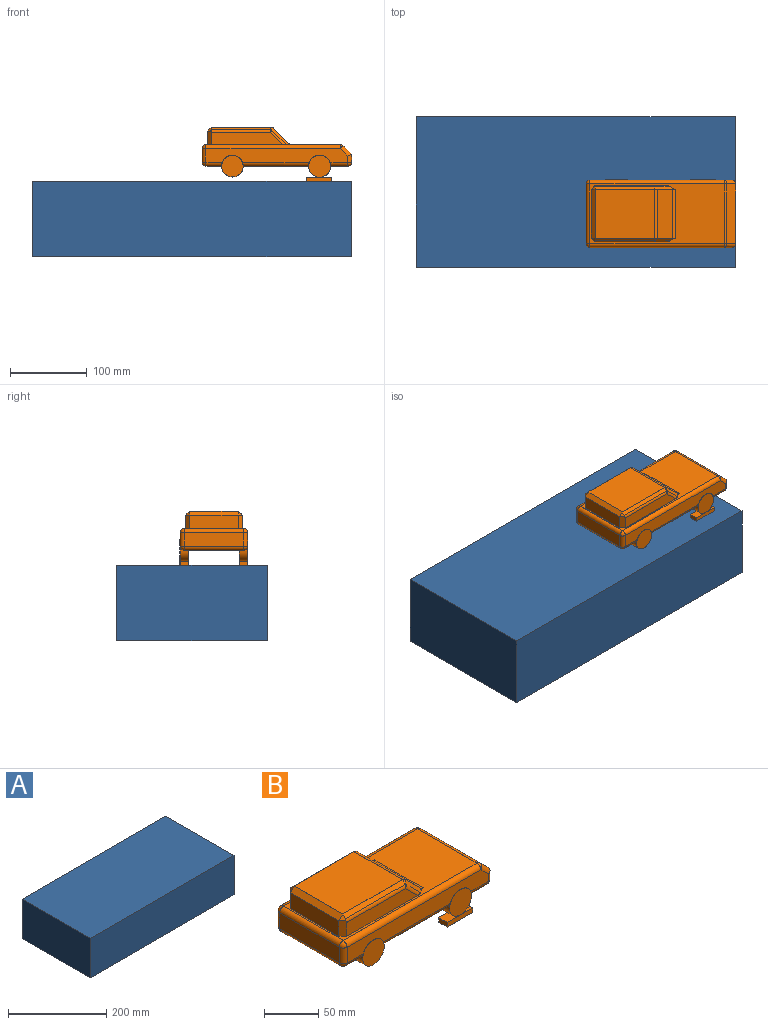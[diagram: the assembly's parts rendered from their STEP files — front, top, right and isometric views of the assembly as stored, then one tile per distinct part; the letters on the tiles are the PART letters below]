
ASSEMBLY  parts=2 mates=1
PART A: 6 faces, bbox 414.3x196x98.3 mm
  f0: plane 414.29x98.32mm, normal (0,-1,0), area 40735mm2, adj f1,f3,f4,f5
  f1: plane 195.96x98.32mm, normal (1,0,0), area 19267.6mm2, adj f0,f2,f4,f5
  f2: plane 414.29x98.32mm, normal (0,1,0), area 40735mm2, adj f1,f3,f4,f5
  f3: plane 195.96x98.32mm, normal (-1,0,0), area 19267.6mm2, adj f0,f2,f4,f5
  f4: plane 414.29x195.96mm, normal (0,0,-1), area 81185.5mm2, adj f0,f1,f2,f3
  f5: plane 414.29x195.96mm, normal (0,0,1), area 81185.5mm2, adj f0,f1,f2,f3
PART B: 166 faces, bbox 195.9x89.8x71.9 mm
  f0: plane 19.88x19.88mm, normal (0.71,0,0.71), area 1mm2, adj f17,f18,f30,f121
  f1: cylinder r=5.08mm len=86.98mm, axis (-1,0,0), area 686.5mm2, adj f3,f8,f72,f75
  f2: cylinder r=5.08mm len=21.19mm, axis (-1,0,0), area 165.3mm2, adj f3,f8,f48,f72
  f3: plane 184.14x77.67mm, normal (0,0,-1), area 13664.9mm2, adj f1,f2,f4,f5,f6,f42,f52,f53
  f4: cylinder r=5.08mm len=86.98mm, axis (1,0,0), area 686.5mm2, adj f3,f10,f61,f64
  f5: cylinder r=5.08mm len=23.05mm, axis (1,0,0), area 180.2mm2, adj f3,f10,f49,f64
  f6: cylinder r=5.08mm len=21.19mm, axis (1,0,0), area 165.3mm2, adj f3,f10,f40,f61
  f7: plane 77.67x10.16mm, normal (1,0,0), area 789.1mm2, adj f32,f43,f53,f58
  f8: plane 184.14x17.78mm, normal (0,1,0), area 2877.3mm2, adj f1,f2,f47,f52,f55,f58,f59,f72
  f9: plane 77.67x17.78mm, normal (-1,0,0), area 1381mm2, adj f39,f42,f46,f47
  f10: plane 184.14x17.78mm, normal (0,-1,0), area 2877.3mm2, adj f4,f5,f6,f39,f43,f44,f45,f61
  f11: plane 175.98x79.23mm, normal (0,0,1), area 5581.3mm2, adj f12,f13,f14,f17,f19,f20,f22,f25
  f12: plane 92.44x15.68mm, normal (0,1,0), area 1326.2mm2, adj f11,f22,f33,f35
  f13: plane 63.17x17.78mm, normal (-1,0,0), area 1123.1mm2, adj f11,f22,f25,f26
  f14: plane 92.44x15.68mm, normal (0,-1,0), area 1326.2mm2, adj f11,f25,f36,f37
  f15: plane 77.63x63.17mm, normal (0,0,1), area 4903.8mm2, adj f18,f23,f26,f28
  f16: plane 19.88x19.88mm, normal (0.71,0,0.71), area 1mm2, adj f17,f18,f20,f131
  f17: cylinder r=5.08mm len=63.17mm, axis (0,-1,0), area 252mm2, adj f0,f11,f16,f19,f31,f151
  f18: cylinder r=5.08mm len=63.17mm, axis (0,-1,0), area 252mm2, adj f0,f15,f16,f21,f29,f150
  f19: cone r=10.16mm half-angle=45deg, axis (0,1,0), area 6.8mm2, adj f11,f17,f20
  f20: plane 22.42x21.37mm, normal (0.5,0.71,0.5), area 141.3mm2, adj f11,f16,f19,f21,f33
  f21: cone r=5.08mm half-angle=45deg, axis (0,-1,0), area 13.1mm2, adj f18,f20,f23,f34
  f22: plane 18.01x5.31mm, normal (-0.71,0.71,0), area 127.3mm2, adj f11,f12,f13,f24,f35
  f23: plane 77.63x3.59mm, normal (0,0.71,0.71), area 394.4mm2, adj f15,f21,f24,f35
  f24: plane 5.31x5.31mm, normal (-0.58,0.58,0.58), area 21.9mm2, adj f22,f23,f26,f35
  f25: plane 18.01x5.31mm, normal (-0.71,-0.71,0), area 127.3mm2, adj f11,f13,f14,f27,f37
  f26: plane 63.17x5.08mm, normal (-0.71,0,0.71), area 453.8mm2, adj f13,f15,f24,f27
  f27: plane 5.31x5.31mm, normal (-0.58,-0.58,0.58), area 21.9mm2, adj f25,f26,f28,f37
  f28: plane 77.63x3.59mm, normal (0,-0.71,0.71), area 394.4mm2, adj f15,f27,f29,f37
  f29: cone r=5.08mm half-angle=45deg, axis (0,1,0), area 13.1mm2, adj f18,f28,f30,f38
  f30: plane 22.42x21.37mm, normal (0.5,-0.71,0.5), area 141.3mm2, adj f0,f11,f29,f31,f36
  f31: cone r=10.16mm half-angle=45deg, axis (0,-1,0), area 6.8mm2, adj f11,f17,f30
  f32: plane 77.67x11.21mm, normal (0.71,0,0.71), area 1231.6mm2, adj f7,f44,f54,f59
  f33: cylinder r=5.08mm len=21.37mm, axis (0.71,0,-0.71), area 97.4mm2, adj f11,f12,f20,f34
  f34: bspline ~3.59x1.92mm, area 1.2mm2, adj f21,f33,f35
  f35: cylinder r=5.08mm len=78.09mm, axis (-1,0,0), area 308.9mm2, adj f12,f22,f23,f24,f34
  f36: cylinder r=5.08mm len=21.37mm, axis (-0.71,0,0.71), area 97.4mm2, adj f11,f14,f30,f38
  f37: cylinder r=5.08mm len=78.09mm, axis (1,0,0), area 308.9mm2, adj f14,f25,f27,f28,f38
  f38: bspline ~3.59x1.92mm, area 1.2mm2, adj f29,f36,f37
  f39: cylinder r=5.08mm len=17.78mm, axis (0,0,1), area 141.9mm2, adj f9,f10,f40,f41
  f40: sphere r=5.08mm, area 40.5mm2, adj f6,f39,f42
  f41: sphere r=5.08mm, area 40.5mm2, adj f39,f45,f46
  f42: cylinder r=5.08mm len=77.67mm, axis (0,-1,0), area 619.8mm2, adj f3,f9,f40,f48
  f43: cylinder r=5.08mm len=10.16mm, axis (0,0,-1), area 72.7mm2, adj f7,f10,f44,f49
  f44: cylinder r=5.08mm len=14.8mm, axis (0.71,0,-0.71), area 118.1mm2, adj f10,f32,f43,f50
  f45: cylinder r=5.08mm len=174.42mm, axis (-1,0,0), area 1391.8mm2, adj f10,f11,f41,f50
  f46: cylinder r=5.08mm len=77.67mm, axis (0,1,0), area 619.8mm2, adj f9,f11,f41,f51
  f47: cylinder r=5.08mm len=17.78mm, axis (0,0,-1), area 141.9mm2, adj f8,f9,f48,f51
  f48: sphere r=5.08mm, area 40.5mm2, adj f2,f42,f47
  f49: sphere r=5.08mm, area 40.5mm2, adj f5,f43,f53
  f50: sphere r=5.08mm, area 20.3mm2, adj f44,f45,f54
  f51: sphere r=5.08mm, area 40.5mm2, adj f46,f47,f55
  f52: cylinder r=5.08mm len=23.05mm, axis (-1,0,0), area 180.2mm2, adj f3,f8,f56,f75
  f53: cylinder r=5.08mm len=77.67mm, axis (0,1,0), area 619.8mm2, adj f3,f7,f49,f56
  f54: cylinder r=5.08mm len=77.67mm, axis (0,-1,0), area 309.9mm2, adj f11,f32,f50,f57
  f55: cylinder r=5.08mm len=174.42mm, axis (1,0,0), area 1391.8mm2, adj f8,f11,f51,f57
  f56: sphere r=5.08mm, area 40.5mm2, adj f52,f53,f58
  f57: sphere r=5.08mm, area 25.4mm2, adj f54,f55,f59
  f58: cylinder r=5.08mm len=10.16mm, axis (0,0,1), area 72.7mm2, adj f7,f8,f56,f59
  f59: cylinder r=5.08mm len=14.8mm, axis (0.71,0,-0.71), area 118.1mm2, adj f8,f32,f57,f58
  f60: plane 28.09x14.04mm, normal (0,1,0), area 309.8mm2, adj f3,f61
  f61: cylinder r=14.04mm len=28.09mm, axis (0,1,0), area 508.2mm2, adj f3,f4,f6,f10,f60,f62
  f62: plane 28.09x28.09mm, normal (0,-1,0), area 619.7mm2, adj f61
  f63: plane 33.02x19.55mm, normal (0,1,0), area 494.8mm2, adj f3,f64,f65,f66,f67,f68,f69
  f64: cylinder r=14.3mm len=28.61mm, axis (0,1,0), area 530.2mm2, adj f3,f4,f5,f10,f63,f65,f69,f70
  f65: plane 17.27x11.08mm, normal (0,0,1), area 191.3mm2, adj f63,f64,f66,f70
  f66: plane 11.08x5.25mm, normal (-1,0,0), area 58.2mm2, adj f63,f65,f67,f70
  f67: plane 33.02x11.08mm, normal (0,0,-1), area 365.8mm2, adj f63,f66,f68,f70
  f68: plane 11.08x5.25mm, normal (1,0,0), area 58.2mm2, adj f63,f67,f69,f70
  f69: plane 15.54x11.08mm, normal (0,0,1), area 172.1mm2, adj f63,f64,f68,f70
  f70: plane 33.86x33.02mm, normal (0,-1,0), area 816.2mm2, adj f64,f65,f66,f67,f68,f69
  f71: plane 28.09x14.04mm, normal (0,-1,0), area 309.8mm2, adj f3,f72
  f72: cylinder r=14.04mm len=28.09mm, axis (0,-1,0), area 506.1mm2, adj f1,f2,f3,f8,f71,f73
  f73: plane 28.09x28.09mm, normal (0,1,0), area 619.7mm2, adj f72
  f74: plane 33.02x19.55mm, normal (0,-1,0), area 494.8mm2, adj f3,f75,f76,f77,f78,f79,f80
  f75: cylinder r=14.3mm len=28.61mm, axis (0,-1,0), area 512.7mm2, adj f1,f3,f8,f52,f74,f76,f80,f81
  f76: plane 17.27x10.69mm, normal (0,0,1), area 184.7mm2, adj f74,f75,f77,f81
  f77: plane 10.69x5.25mm, normal (-1,0,0), area 56.1mm2, adj f74,f76,f78,f81
  f78: plane 33.02x10.69mm, normal (0,0,-1), area 353.1mm2, adj f74,f77,f79,f81
  f79: plane 10.69x5.25mm, normal (1,0,0), area 56.1mm2, adj f74,f78,f80,f81
  f80: plane 15.54x10.69mm, normal (0,0,1), area 166.1mm2, adj f74,f75,f79,f81
  f81: plane 33.86x33.02mm, normal (0,1,0), area 816.2mm2, adj f75,f76,f77,f78,f79,f80
  f82: plane 28.56x28.56mm, normal (0,-1,0), area 640.5mm2, adj f83
  f83: cylinder r=14.28mm len=28.56mm, axis (0,-1,0), area 512.1mm2, adj f82,f99,f142,f147,f149,f153
  f84: plane 28.04x28.04mm, normal (0,-1,0), area 617.4mm2, adj f85
  f85: cylinder r=14.02mm len=28.04mm, axis (0,-1,0), area 503.3mm2, adj f84,f86,f142,f147,f148,f149
  f86: plane 28.04x14.04mm, normal (0,1,0), area 309.4mm2, adj f85,f147
  f87: plane 28.56x28.56mm, normal (0,1,0), area 640.5mm2, adj f88
  f88: cylinder r=14.28mm len=28.56mm, axis (0,1,0), area 514.6mm2, adj f87,f140,f145,f146,f147,f152
  f89: plane 28.04x28.04mm, normal (0,1,0), area 617.4mm2, adj f90
  f90: cylinder r=14.02mm len=28.04mm, axis (0,1,0), area 505.5mm2, adj f89,f91,f140,f144,f146,f147
  f91: plane 28.04x14.04mm, normal (0,-1,0), area 309.4mm2, adj f90,f147
  f92: cylinder r=5.05mm len=14.78mm, axis (0.71,0,-0.71), area 117.5mm2, adj f93,f94,f119,f142
  f93: cylinder r=5.05mm len=10.15mm, axis (0,0,1), area 72.3mm2, adj f92,f95,f142,f143
  f94: sphere r=5.05mm, area 25.2mm2, adj f92,f96,f97
  f95: sphere r=5.05mm, area 40.1mm2, adj f93,f98,f99
  f96: cylinder r=5.05mm len=174.42mm, axis (1,0,0), area 1384.8mm2, adj f94,f100,f139,f142
  f97: cylinder r=5.05mm len=77.67mm, axis (0,-1,0), area 308.3mm2, adj f94,f101,f119,f139
  f98: cylinder r=5.05mm len=77.67mm, axis (0,1,0), area 616.7mm2, adj f95,f102,f143,f147
  f99: cylinder r=5.05mm len=23.07mm, axis (-1,0,0), area 179.5mm2, adj f83,f95,f142,f147
  f100: sphere r=5.05mm, area 40.1mm2, adj f96,f104,f105
  f101: sphere r=5.05mm, area 20.1mm2, adj f97,f106,f107
  f102: sphere r=5.05mm, area 40.1mm2, adj f98,f108,f145
  f103: sphere r=5.05mm, area 40.1mm2, adj f104,f109,f148
  f104: cylinder r=5.05mm len=17.78mm, axis (0,0,-1), area 141.2mm2, adj f100,f103,f141,f142
  f105: cylinder r=5.05mm len=77.67mm, axis (0,1,0), area 616.7mm2, adj f100,f110,f139,f141
  f106: cylinder r=5.05mm len=174.42mm, axis (-1,0,0), area 1384.8mm2, adj f101,f110,f139,f140
  f107: cylinder r=5.05mm len=14.78mm, axis (0.71,0,-0.71), area 117.5mm2, adj f101,f108,f119,f140
  f108: cylinder r=5.05mm len=10.15mm, axis (0,0,-1), area 72.3mm2, adj f102,f107,f140,f143
  f109: cylinder r=5.05mm len=77.67mm, axis (0,-1,0), area 616.7mm2, adj f103,f111,f141,f147
  f110: sphere r=5.05mm, area 40.1mm2, adj f105,f106,f112
  f111: sphere r=5.05mm, area 40.1mm2, adj f109,f112,f144
  f112: cylinder r=5.05mm len=17.78mm, axis (0,0,1), area 141.2mm2, adj f110,f111,f140,f141
  f113: offset ~3.64x1.97mm, area 1.2mm2, adj f114,f115,f122
  f114: cylinder r=5.05mm len=78.08mm, axis (1,0,0), area 307.3mm2, adj f113,f123,f124,f126,f136
  f115: cylinder r=5.05mm len=21.37mm, axis (-0.71,0,0.71), area 97mm2, adj f113,f121,f136,f139
  f116: cylinder r=5.05mm len=78.08mm, axis (-1,0,0), area 307.3mm2, adj f117,f127,f128,f129,f138
  f117: offset ~3.64x1.97mm, area 1.2mm2, adj f116,f118,f130
  f118: cylinder r=5.05mm len=21.37mm, axis (0.71,0,-0.71), area 97mm2, adj f117,f131,f138,f139
  f119: plane 77.67x11.2mm, normal (-0.71,0,-0.71), area 1230.7mm2, adj f92,f97,f107,f143
  f120: cone r=10.18mm half-angle=45deg, axis (0,-1,0), area 6.8mm2, adj f121,f134,f139
  f121: plane 22.44x21.4mm, normal (-0.5,0.71,-0.5), area 142mm2, adj f0,f115,f120,f122,f139,f150,f151
  f122: cone r=5.06mm half-angle=45deg, axis (0,1,0), area 13mm2, adj f113,f121,f123,f133
  f123: plane 77.63x3.59mm, normal (0,0.71,-0.71), area 393.4mm2, adj f114,f122,f124,f135
  f124: plane 5.29x5.29mm, normal (0.58,0.58,-0.58), area 21.8mm2, adj f114,f123,f125,f126
  f125: plane 63.15x5.07mm, normal (0.71,0,-0.71), area 452.1mm2, adj f124,f127,f135,f137
  f126: plane 18.02x5.29mm, normal (0.71,0.71,0), area 127mm2, adj f114,f124,f136,f137,f139
  f127: plane 5.29x5.29mm, normal (0.58,-0.58,-0.58), area 21.8mm2, adj f116,f125,f128,f129
  f128: plane 77.63x3.59mm, normal (0,-0.71,-0.71), area 393.5mm2, adj f116,f127,f130,f135
  f129: plane 18.02x5.29mm, normal (0.71,-0.71,0), area 127mm2, adj f116,f127,f137,f138,f139
  f130: cone r=5.06mm half-angle=45deg, axis (0,-1,0), area 13mm2, adj f117,f128,f131,f133
  f131: plane 22.44x21.4mm, normal (-0.5,-0.71,-0.5), area 142mm2, adj f16,f118,f130,f132,f139,f150,f151
  f132: cone r=10.18mm half-angle=45deg, axis (0,1,0), area 6.8mm2, adj f131,f134,f139
  f133: cylinder r=5.05mm len=63.15mm, axis (0,-1,0), area 250.7mm2, adj f122,f130,f135,f150
  f134: cylinder r=5.11mm len=63.15mm, axis (0,-1,0), area 253.2mm2, adj f120,f132,f139,f151
  f135: plane 77.63x63.15mm, normal (0,0,-1), area 4901.5mm2, adj f123,f125,f128,f133
  f136: plane 92.45x15.7mm, normal (0,1,0), area 1328.3mm2, adj f114,f115,f126,f139
  f137: plane 63.15x17.8mm, normal (1,0,0), area 1123.7mm2, adj f125,f126,f129,f139
  f138: plane 92.45x15.7mm, normal (0,-1,0), area 1328.3mm2, adj f116,f118,f129,f139
  f139: plane 175.99x79.25mm, normal (0,0,-1), area 5588.4mm2, adj f96,f97,f105,f106,f115,f118,f120,f121
  f140: plane 184.14x17.78mm, normal (0,1,0), area 2879mm2, adj f88,f90,f106,f107,f108,f112,f144,f145
  f141: plane 77.67x17.78mm, normal (1,0,0), area 1381mm2, adj f104,f105,f109,f112
  f142: plane 184.14x17.78mm, normal (0,-1,0), area 2879mm2, adj f83,f85,f92,f93,f96,f99,f104,f148
  f143: plane 77.67x10.15mm, normal (-1,0,0), area 788.3mm2, adj f93,f98,f108,f119
  f144: cylinder r=5.05mm len=21.22mm, axis (1,0,0), area 164.7mm2, adj f90,f111,f140,f147
  f145: cylinder r=5.05mm len=23.07mm, axis (1,0,0), area 179.5mm2, adj f88,f102,f140,f147
  f146: cylinder r=5.05mm len=87.03mm, axis (1,0,0), area 683.5mm2, adj f88,f90,f140,f147
  f147: plane 184.14x77.67mm, normal (0,0,1), area 13669mm2, adj f83,f85,f86,f88,f90,f91,f98,f99
  f148: cylinder r=5.05mm len=21.22mm, axis (-1,0,0), area 164.7mm2, adj f85,f103,f142,f147
  f149: cylinder r=5.05mm len=87.03mm, axis (-1,0,0), area 683.5mm2, adj f83,f85,f142,f147
  f150: plane 63.15x0.02mm, normal (0.71,0,-0.71), area 1.6mm2, adj f18,f121,f131,f133
  f151: plane 63.15x0.02mm, normal (-0.71,0,0.71), area 1.6mm2, adj f17,f121,f131,f134
  f152: plane 28.56x14.3mm, normal (0,-1,0), area 321mm2, adj f88,f147
  f153: plane 28.56x14.3mm, normal (0,1,0), area 321mm2, adj f83,f147
  f154: plane 32.97x5.2mm, normal (0,1,0), area 171.4mm2, adj f156,f157,f158,f159
  f155: plane 32.97x5.2mm, normal (0,-1,0), area 171.4mm2, adj f156,f157,f158,f159
  f156: plane 32.97x11.03mm, normal (0,0,-1), area 363.6mm2, adj f154,f155,f157,f159
  f157: plane 11.03x5.2mm, normal (1,0,0), area 57.3mm2, adj f154,f155,f156,f158
  f158: plane 32.97x11.03mm, normal (0,0,1), area 363.6mm2, adj f154,f155,f157,f159
  f159: plane 11.03x5.2mm, normal (-1,0,0), area 57.3mm2, adj f154,f155,f156,f158
  f160: plane 32.97x10.64mm, normal (0,0,-1), area 350.9mm2, adj f161,f163,f164,f165
  f161: plane 10.64x5.2mm, normal (-1,0,0), area 55.3mm2, adj f160,f162,f164,f165
  f162: plane 32.97x10.64mm, normal (0,0,1), area 350.9mm2, adj f161,f163,f164,f165
  f163: plane 10.64x5.2mm, normal (1,0,0), area 55.3mm2, adj f160,f162,f164,f165
  f164: plane 32.97x5.2mm, normal (0,1,0), area 171.4mm2, adj f160,f161,f162,f163
  f165: plane 32.97x5.2mm, normal (0,-1,0), area 171.4mm2, adj f160,f161,f162,f163
PLACE A t=(16.01,0,0)mm fixed
PLACE B t=(126.45,-28.48,-18.02)mm
MATE slider B.f67 <-> A.f5  axis (0,0,1) through (197.75,-72.58,-37.57)mm
